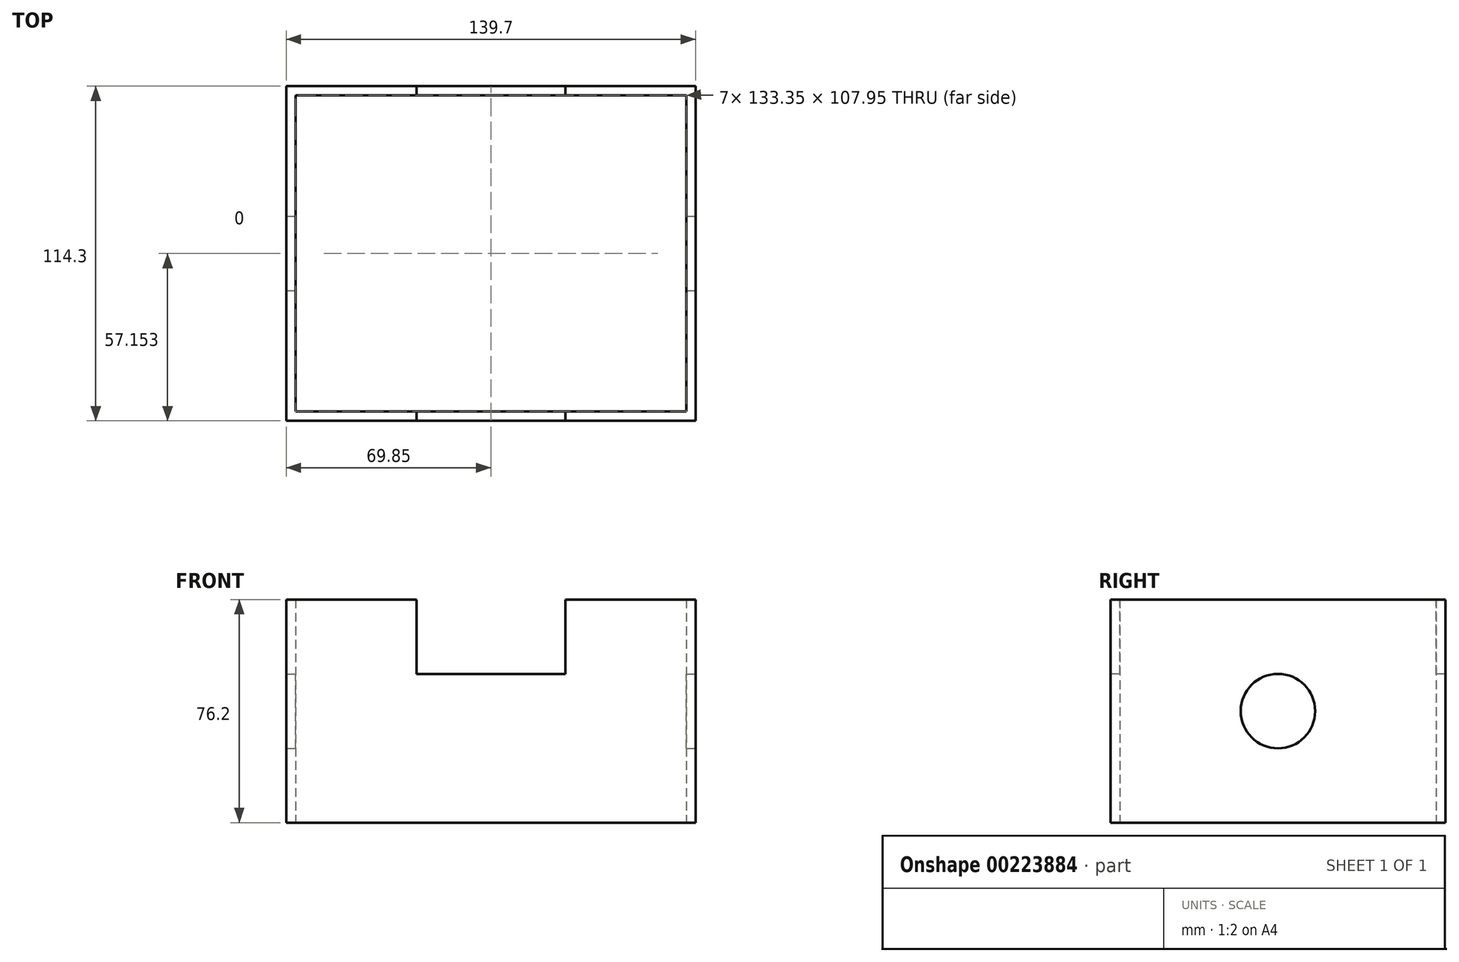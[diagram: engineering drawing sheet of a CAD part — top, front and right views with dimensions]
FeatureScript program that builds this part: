
annotation { "Feature Type Name" : "Feature", "Feature Type Description" : "" }
export const myFeature = defineFeature(function(context is Context, id is Id, definition is map)
    precondition{}
    {
        {
            var Q0;
            Q0=qCreatedBy(makeId("Top.planeOp"),FACE);
            var sketch = newSketch(context, id + "F0", { "sketchPlane" : qUnion([Q0])});
            skPoint(sketch, "E0.middle", {"position": v(0, 0) * mm});
            skLineSegment(sketch, "E1.bottom", {"start": v(69.85, 50.33) * mm, "end": v(-69.85, 50.33) * mm});
            skLineSegment(sketch, "E1.top", {"start": v(69.85, -63.97) * mm, "end": v(-69.85, -63.97) * mm});
            skLineSegment(sketch, "E1.left", {"start": v(69.85, 50.33) * mm, "end": v(69.85, -63.97) * mm});
            skLineSegment(sketch, "E1.right", {"start": v(-69.85, 50.33) * mm, "end": v(-69.85, -63.97) * mm});
            skPoint(sketch, "E1.middle", {"position": v(0, -6.82) * mm});
            skLineSegment(sketch, "E2.bottom", {"start": v(66.68, 47.16) * mm, "end": v(-66.68, 47.16) * mm});
            skLineSegment(sketch, "E2.top", {"start": v(66.68, -60.8) * mm, "end": v(-66.68, -60.8) * mm});
            skLineSegment(sketch, "E2.left", {"start": v(66.68, 47.16) * mm, "end": v(66.68, -60.8) * mm});
            skLineSegment(sketch, "E2.right", {"start": v(-66.68, 47.16) * mm, "end": v(-66.68, -60.8) * mm});
            skSolve(sketch);
        }
        {
            var Q0;
            Q0=makeQuery(id+"F0.imprint","IMPRINT",FACE,{"disambiguationData":[TD([[makeQuery(id+"F0.imprint","IMPRINT",EDGE,{"derivedFrom":sQuery(id+"F0.wireOp",EDGE,"E1.bottom")}),1.0]])]});
            extrude(context, id + "F1", {"entities" : qUnion([Q0]), "depth" : 76.2 * mm});
        }
        {
            var Q0;
            Q0=makeQuery(id+"F1.opExtrude","SWEPT_FACE",FACE,{"disambiguationData":[OSD([sQuery(id+"F0.wireOp",EDGE,"E1.top")])]});
            var sketch = newSketch(context, id + "F2", { "sketchPlane" : qUnion([Q0])});
            skLineSegment(sketch, "E3.bottom", {"start": v(25.4, 50.8) * mm, "end": v(-25.4, 50.8) * mm});
            skLineSegment(sketch, "E3.top", {"start": v(25.4, 101.6) * mm, "end": v(-25.4, 101.6) * mm});
            skLineSegment(sketch, "E3.left", {"start": v(25.4, 50.8) * mm, "end": v(25.4, 101.6) * mm});
            skLineSegment(sketch, "E3.right", {"start": v(-25.4, 50.8) * mm, "end": v(-25.4, 101.6) * mm});
            skPoint(sketch, "E3.middle", {"position": v(0, 76.2) * mm});
            skSolve(sketch);
        }
        {
            var Q0;
            Q0 = qSketchRegion(id + "F2", true);
            extrude(context, id + "F3", {"entities" : qUnion([Q0]), "operationType" : NewBodyOperationType.REMOVE, "oppositeDirection" : true, "depth" : 127 * mm});
        }
        {
            var Q0;
            Q0=makeQuery(id+"F1.opExtrude","SWEPT_FACE",FACE,{"disambiguationData":[OSD([sQuery(id+"F0.wireOp",EDGE,"E1.left")])]});
            var sketch = newSketch(context, id + "F4", { "sketchPlane" : qUnion([Q0])});
            skLineSegment(sketch, "E4", {"start": v(50.33, 0) * mm, "end": v(50.33, 76.2) * mm});
            skCircle(sketch, "E5", {"center": v(-6.82, 38.1) * mm, "radius": 12.7 * mm});
            skSolve(sketch);
        }
        {
            var Q0;
            Q0=makeQuery(id+"F4.imprint","IMPRINT",FACE,{"disambiguationData":[TD([[makeQuery(id+"F4.imprint","IMPRINT",EDGE,{"derivedFrom":sQuery(id+"F4.wireOp",EDGE,"E5")}),1.0]])]});
            extrude(context, id + "F5", {"entities" : qUnion([Q0]), "operationType" : NewBodyOperationType.REMOVE, "oppositeDirection" : true, "depth" : 175.77 * mm});
        }
    });
